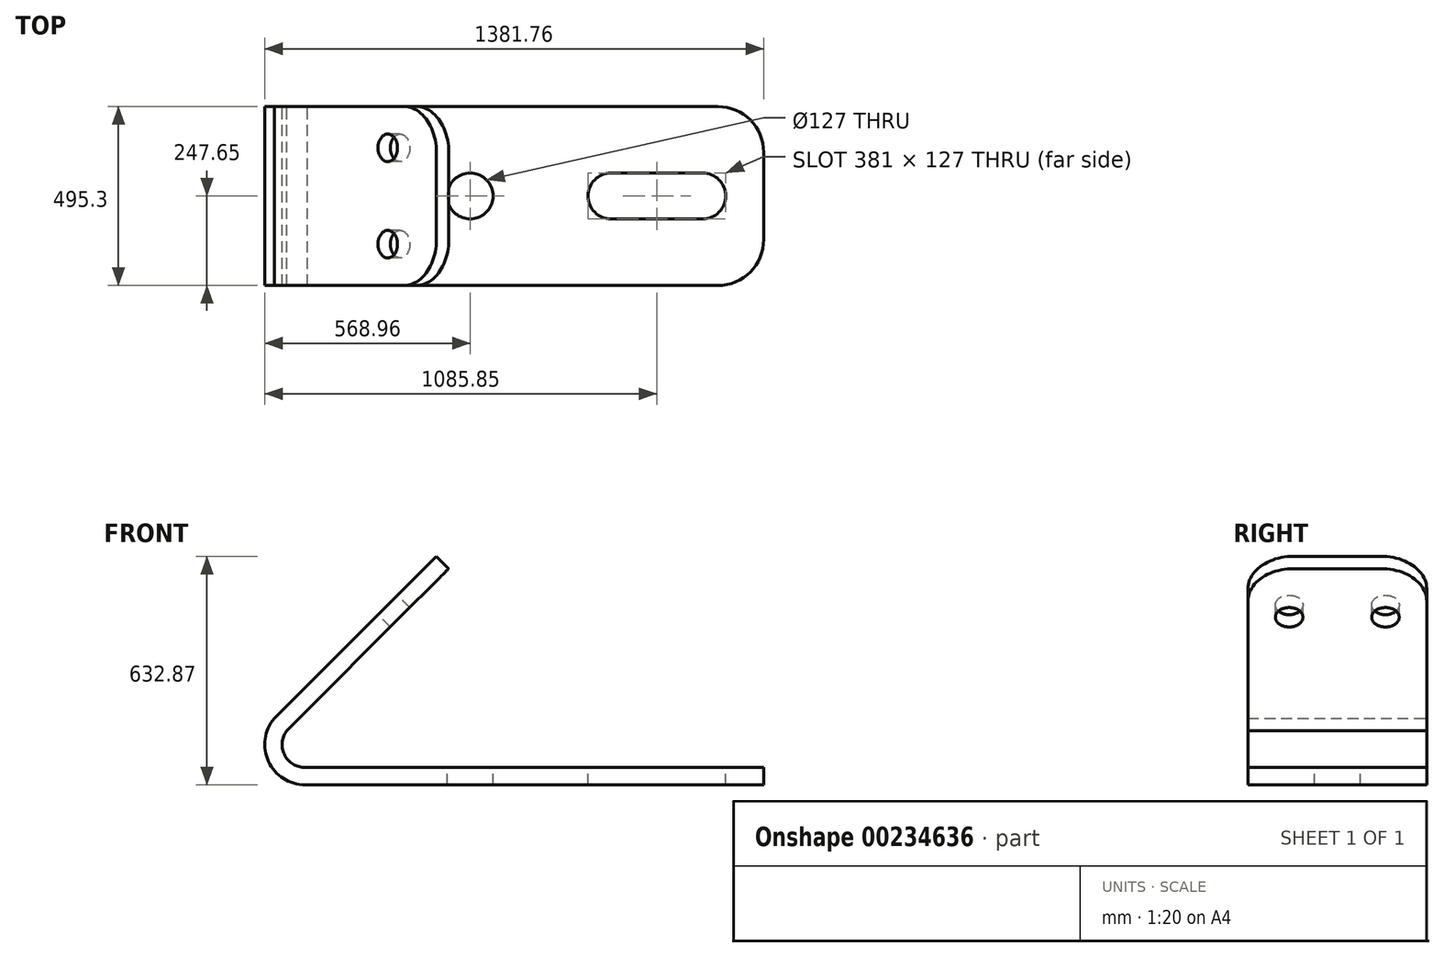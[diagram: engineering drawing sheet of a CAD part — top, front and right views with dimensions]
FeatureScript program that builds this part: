
annotation { "Feature Type Name" : "Feature", "Feature Type Description" : "" }
export const myFeature = defineFeature(function(context is Context, id is Id, definition is map)
    precondition{}
    {
        {
            var Q0;
            Q0=qCreatedBy(makeId("Front.planeOp"),FACE);
            var sketch = newSketch(context, id + "F0", { "sketchPlane" : qUnion([Q0])});
            skLineSegment(sketch, "E0", {"start": v(0, 0) * mm, "end": v(1270, 0) * mm});
            skLineSegment(sketch, "E1", {"start": v(1270, 0) * mm, "end": v(1270, 48.26) * mm});
            skLineSegment(sketch, "E2", {"start": v(1270, 48.26) * mm, "end": v(0, 48.26) * mm});
            skArc(sketch, "E3", {"start": v(0, 0) * mm, "mid": v(-101.36, 64.68) * mm, "end": v(-85.4, 183.86) * mm});
            skLineSegment(sketch, "E4", {"start": v(-85.4, 183.86) * mm, "end": v(363.62, 632.87) * mm});
            skLineSegment(sketch, "E5", {"start": v(363.62, 632.87) * mm, "end": v(397.74, 598.75) * mm});
            skLineSegment(sketch, "E6", {"start": v(397.74, 598.75) * mm, "end": v(-51.26, 149.74) * mm});
            skArc(sketch, "E7", {"start": v(-51.26, 149.74) * mm, "mid": v(-55.52, 80.33) * mm, "end": v(6.17, 48.26) * mm});
            skSolve(sketch);
        }
        {
            var Q0;
            Q0 = qSketchRegion(id + "F0", true);
            extrude(context, id + "F1", {"entities" : qUnion([Q0]), "endBound" : BoundingType.SYMMETRIC, "depth" : 495.3 * mm});
        }
        {
            var Q0;
            Q0=makeQuery(id+"F1.opExtrude","SWEPT_FACE",FACE,{"disambiguationData":[OSD([sQuery(id+"F0.wireOp",EDGE,"E2")])]});
            var sketch = newSketch(context, id + "F2", { "sketchPlane" : qUnion([Q0])});
            skLineSegment(sketch, "E8", {"start": v(1270, 0) * mm, "end": v(457.2, 0) * mm, "construction": true});
            skPoint(sketch, "E8.endSnap0", {"position": v(6.17, 0) * mm});
            skCircle(sketch, "E9", {"center": v(457.2, 0) * mm, "radius": 63.5 * mm});
            skLineSegment(sketch, "E10.bottom", {"start": v(847.09, 63.5) * mm, "end": v(1101.09, 63.5) * mm});
            skLineSegment(sketch, "E10.top", {"start": v(847.09, -63.5) * mm, "end": v(1101.09, -63.5) * mm});
            skLineSegment(sketch, "E10.left", {"start": v(847.09, 63.5) * mm, "end": v(847.09, -63.5) * mm});
            skLineSegment(sketch, "E10.right", {"start": v(1101.09, 63.5) * mm, "end": v(1101.09, -63.5) * mm});
            skPoint(sketch, "E10.middle", {"position": v(974.09, 0) * mm});
            skArc(sketch, "E11", {"start": v(847.09, 63.5) * mm, "mid": v(783.59, 0) * mm, "end": v(847.09, -63.5) * mm});
            skArc(sketch, "E12", {"start": v(1101.09, -63.5) * mm, "mid": v(1164.59, 0) * mm, "end": v(1101.09, 63.5) * mm});
            skSolve(sketch);
        }
        {
            var Q0;
            Q0 = qSketchRegion(id + "F2", true);
            extrude(context, id + "F3", {"entities" : qUnion([Q0]), "operationType" : NewBodyOperationType.REMOVE, "endBound" : BoundingType.THROUGH_ALL, "oppositeDirection" : true, "depth" : 25.4 * mm});
        }
        {
            var Q0;
            Q0=makeQuery(id+"F1.opExtrude","SWEPT_FACE",FACE,{"disambiguationData":[OSD([sQuery(id+"F0.wireOp",EDGE,"E4")])]});
            var sketch = newSketch(context, id + "F4", { "sketchPlane" : qUnion([Q0])});
            skLineSegment(sketch, "E13", {"start": v(-133.35, 704.63) * mm, "end": v(-133.35, 69.63) * mm, "construction": true});
            skLineSegment(sketch, "E14", {"start": v(133.35, 704.63) * mm, "end": v(133.35, 69.63) * mm, "construction": true});
            skCircle(sketch, "E15", {"center": v(-133.35, 514.13) * mm, "radius": 38.1 * mm});
            skCircle(sketch, "E16", {"center": v(133.35, 514.13) * mm, "radius": 38.1 * mm});
            skSolve(sketch);
        }
        {
            var Q0;
            Q0=makeQuery(id+"F4.imprint","IMPRINT",FACE,{"disambiguationData":[TD([[makeQuery(id+"F4.imprint","IMPRINT",EDGE,{"derivedFrom":sQuery(id+"F4.wireOp",EDGE,"E15")}),1.0]])]});
            var Q1;
            Q1=makeQuery(id+"F4.imprint","IMPRINT",FACE,{"disambiguationData":[TD([[makeQuery(id+"F4.imprint","IMPRINT",EDGE,{"derivedFrom":sQuery(id+"F4.wireOp",EDGE,"E16")}),1.0]])]});
            extrude(context, id + "F5", {"entities" : qUnion([Q0, Q1]), "operationType" : NewBodyOperationType.REMOVE, "oppositeDirection" : true, "depth" : 218.44 * mm});
        }
        {
            var Q0;
            Q0=makeQuery(id+"F1.opExtrude","CAP_EDGE",EDGE,{"disambiguationData":[OSD([sQuery(id+"F0.wireOp",EDGE,"E5")])],"isStart":false});
            var Q1;
            Q1=makeQuery(id+"F1.opExtrude","CAP_EDGE",EDGE,{"disambiguationData":[OSD([sQuery(id+"F0.wireOp",EDGE,"E5")])],"isStart":true});
            var Q2;
            Q2=makeQuery(id+"F1.opExtrude","CAP_EDGE",EDGE,{"disambiguationData":[OSD([sQuery(id+"F0.wireOp",EDGE,"E1")])],"isStart":true});
            var Q3;
            Q3=makeQuery(id+"F1.opExtrude","CAP_EDGE",EDGE,{"disambiguationData":[OSD([sQuery(id+"F0.wireOp",EDGE,"E1")])],"isStart":false});
            fillet(context, id + "F6", {"entities" : qUnion([Q0, Q1, Q2, Q3]), "radius" : 127 * mm, "tangentPropagation" : true, "allowEdgeOverflow" : false});
        }
    });
